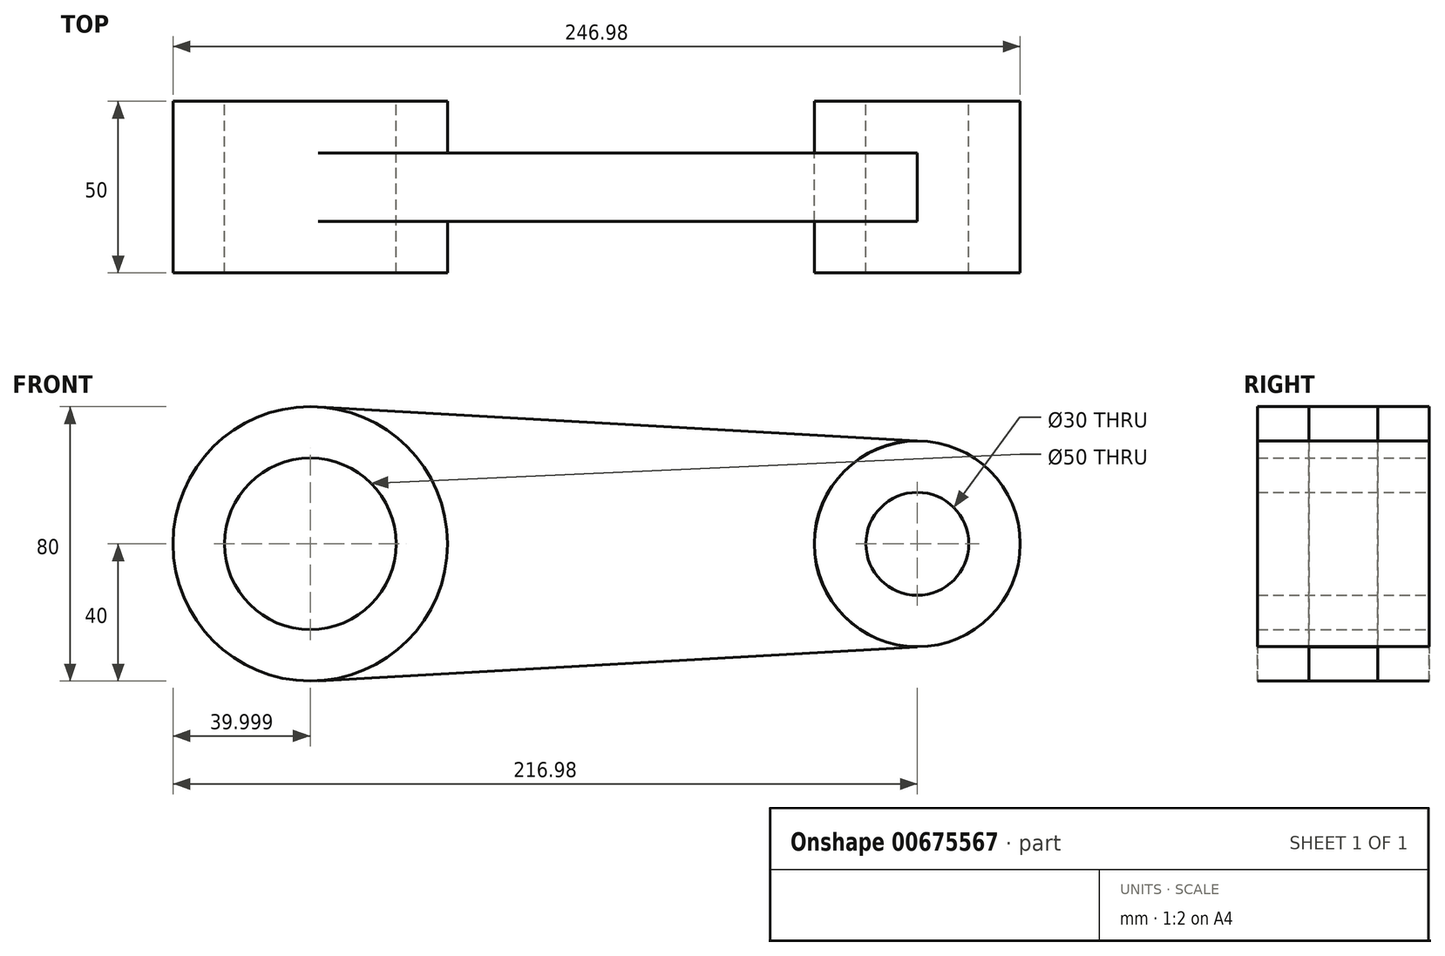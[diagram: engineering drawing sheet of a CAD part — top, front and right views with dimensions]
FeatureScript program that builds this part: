
annotation { "Feature Type Name" : "Feature", "Feature Type Description" : "" }
export const myFeature = defineFeature(function(context is Context, id is Id, definition is map)
    precondition{}
    {
        {
            var Q0;
            Q0=qCreatedBy(makeId("Front.planeOp"),FACE);
            var sketch = newSketch(context, id + "F0", { "sketchPlane" : qUnion([Q0])});
            skCircle(sketch, "E0", {"center": v(0, 0) * mm, "radius": 15 * mm});
            skCircle(sketch, "E1", {"center": v(0, 0) * mm, "radius": 30 * mm});
            skCircle(sketch, "E2", {"center": v(-176.98, 0) * mm, "radius": 25 * mm});
            skCircle(sketch, "E3", {"center": v(-176.98, 0) * mm, "radius": 40 * mm});
            skLineSegment(sketch, "E4", {"start": v(-174.72, 39.94) * mm, "end": v(0, 30.05) * mm});
            skLineSegment(sketch, "E5", {"start": v(-174.72, -39.94) * mm, "end": v(0, -30.05) * mm});
            skArc(sketch, "E6", {"start": v(-174.72, -39.94) * mm, "mid": v(-136.98, 0) * mm, "end": v(-174.72, 39.94) * mm});
            skArc(sketch, "E7", {"start": v(0, 30.05) * mm, "mid": v(-30.05, 0) * mm, "end": v(0, -30.05) * mm});
            skSolve(sketch);
        }
        {
            var Q0;
            {var subQ0=sQuery(id+"F0.wireOp",EDGE,"E4");Q0=makeQuery(id+"F0.imprint","IMPRINT",FACE,{"disambiguationData":[TD([[makeQuery(id+"F0.imprint","IMPRINT",EDGE,{"derivedFrom":subQ0}),-1.0]])]});}
            extrude(context, id + "F1", {"entities" : qUnion([Q0]), "depth" : 20 * mm, "offsetDistance" : 25 * mm});
        }
        {
            var Q0;
            Q0=makeQuery(id+"F0.imprint","IMPRINT",FACE,{"disambiguationData":[TD([[makeQuery(id+"F0.imprint","IMPRINT",EDGE,{"derivedFrom":sQuery(id+"F0.wireOp",EDGE,"E2")}),-1.0]])]});
            var Q1;
            Q1=makeQuery(id+"F0.imprint","IMPRINT",FACE,{"disambiguationData":[TD([[makeQuery(id+"F0.imprint","IMPRINT",EDGE,{"derivedFrom":sQuery(id+"F0.wireOp",EDGE,"E0")}),-1.0]])]});
            extrude(context, id + "F2", {"entities" : qUnion([Q0, Q1]), "operationType" : NewBodyOperationType.ADD, "depth" : 35 * mm, "offsetDistance" : 25 * mm});
        }
        {
            var Q0;
            Q0=makeQuery(id+"F2.opExtrude","CAP_FACE",FACE,{"disambiguationData":[OSD([sQuery(id+"F0.wireOp",EDGE,"E0"),sQuery(id+"F0.wireOp",EDGE,"E1")])],"isStart":true});
            var sketch = newSketch(context, id + "F3", { "sketchPlane" : qUnion([Q0])});
            skCircle(sketch, "E8", {"center": v(0, 0) * mm, "radius": 30 * mm});
            skCircle(sketch, "E9", {"center": v(0, 0) * mm, "radius": 15 * mm});
            skSolve(sketch);
        }
        {
            var Q0;
            Q0 = qSketchRegion(id + "F3", true);
            extrude(context, id + "F4", {"entities" : qUnion([Q0]), "operationType" : NewBodyOperationType.ADD, "depth" : 15 * mm, "offsetDistance" : 25 * mm});
        }
        {
            var Q0;
            {var subQ0=sQuery(id+"F0.wireOp",EDGE,"E3");Q0=makeQuery(id+"F2.boolean.opBoolean","MERGE",FACE,{"derivedFrom":[makeQuery(id+"F1.opExtrude","CAP_FACE",FACE,{"disambiguationData":[OSD([subQ0,sQuery(id+"F0.wireOp",EDGE,"E4"),sQuery(id+"F0.wireOp",EDGE,"E5"),sQuery(id+"F0.wireOp",EDGE,"E7")])],"isStart":true}),makeQuery(id+"F2.opExtrude","CAP_FACE",FACE,{"disambiguationData":[OSD([sQuery(id+"F0.wireOp",EDGE,"E2"),subQ0])],"isStart":true})]});}
            var sketch = newSketch(context, id + "F5", { "sketchPlane" : qUnion([Q0])});
            skCircle(sketch, "E10", {"center": v(176.98, 0) * mm, "radius": 25 * mm});
            skCircle(sketch, "E11", {"center": v(176.98, 0) * mm, "radius": 40 * mm});
            skSolve(sketch);
        }
        {
            var Q0;
            Q0 = qSketchRegion(id + "F5", true);
            extrude(context, id + "F6", {"entities" : qUnion([Q0]), "operationType" : NewBodyOperationType.ADD, "depth" : 15 * mm, "offsetDistance" : 25 * mm});
        }
    });
